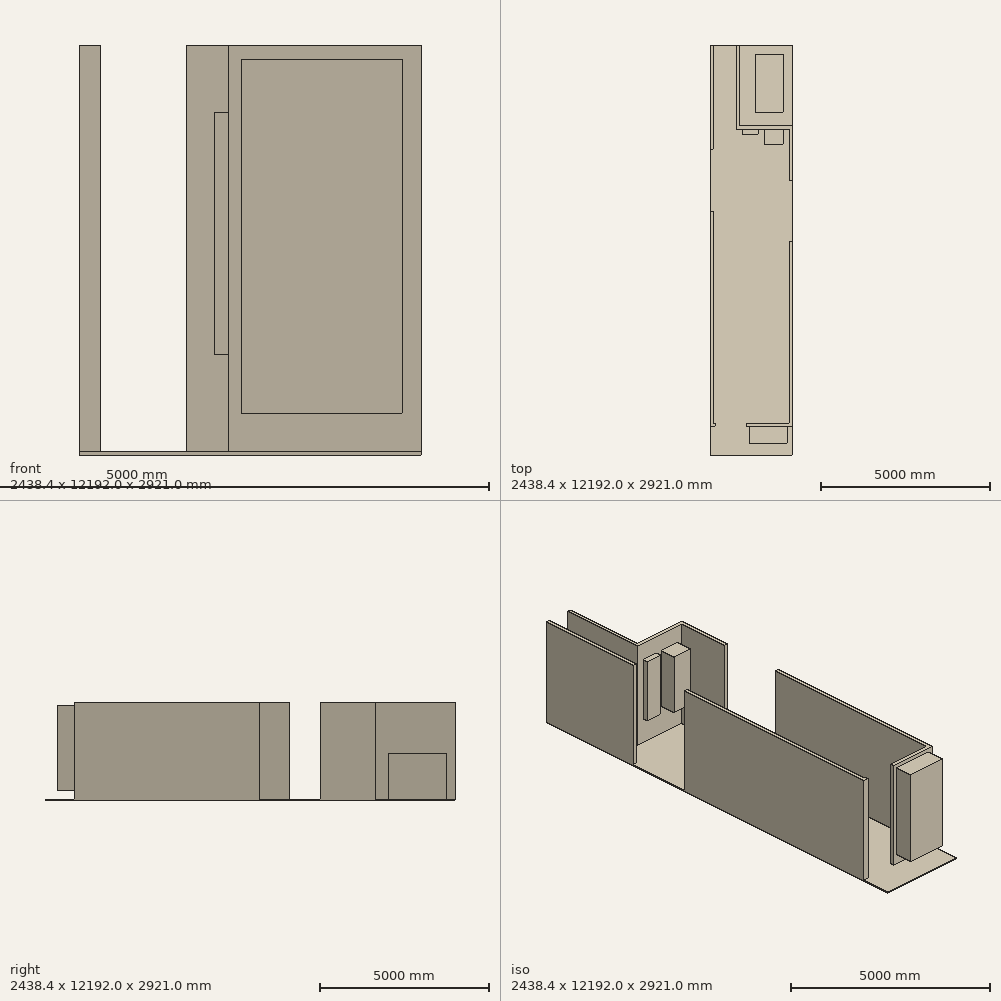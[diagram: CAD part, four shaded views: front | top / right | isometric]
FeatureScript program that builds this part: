
annotation { "Feature Type Name" : "Feature", "Feature Type Description" : "" }
export const myFeature = defineFeature(function(context is Context, id is Id, definition is map)
    precondition{}
    {
        {
            var Q0;
            Q0=qCreatedBy(makeId("Top.planeOp"),FACE);
            var sketch = newSketch(context, id + "F0", { "sketchPlane" : qUnion([Q0])});
            skLineSegment(sketch, "E0.bottom", {"start": v(0, 0) * mm, "end": v(2438.4, 0) * mm});
            skLineSegment(sketch, "E0.top", {"start": v(0, 12192) * mm, "end": v(2438.4, 12192) * mm});
            skLineSegment(sketch, "E0.left", {"start": v(0, 0) * mm, "end": v(0, 12192) * mm});
            skLineSegment(sketch, "E0.right", {"start": v(2438.4, 0) * mm, "end": v(2438.4, 12192) * mm});
            skSolve(sketch);
        }
        {
            var Q0;
            Q0=makeQuery(id+"F0.imprint","IMPRINT",FACE,{"disambiguationData":[TD([[makeQuery(id+"F0.imprint","IMPRINT",EDGE,{"derivedFrom":sQuery(id+"F0.wireOp",EDGE,"E0.bottom")}),1.0]])]});
            extrude(context, id + "F1", {"entities" : qUnion([Q0]), "depth" : 25.4 * mm, "offsetDistance" : 25.4 * mm});
        }
        {
            var Q0;
            Q0=makeQuery(id+"F1.opExtrude","CAP_FACE",FACE,{"disambiguationData":[OSD([sQuery(id+"F0.wireOp",EDGE,"E0.bottom"),sQuery(id+"F0.wireOp",EDGE,"E0.top"),sQuery(id+"F0.wireOp",EDGE,"E0.left"),sQuery(id+"F0.wireOp",EDGE,"E0.right")])],"isStart":false});
            var sketch = newSketch(context, id + "F2", { "sketchPlane" : qUnion([Q0])});
            skLineSegment(sketch, "E1.0", {"start": v(0, 0) * mm, "end": v(0, 7264.4) * mm});
            skLineSegment(sketch, "E2.0", {"start": v(0, 12192) * mm, "end": v(2438.4, 12192) * mm});
            skLineSegment(sketch, "E2.1", {"start": v(2438.4, 0) * mm, "end": v(2438.4, 6350) * mm});
            skLineSegment(sketch, "E2.2", {"start": v(0, 0) * mm, "end": v(2438.4, 0) * mm});
            skLineSegment(sketch, "E3.1", {"start": v(101.6, 965.2) * mm, "end": v(101.6, 7264.4) * mm});
            skLineSegment(sketch, "E4", {"start": v(0, 863.6) * mm, "end": v(149.81, 863.6) * mm});
            skLineSegment(sketch, "E5", {"start": v(762, 12192) * mm, "end": v(762, 9702.8) * mm});
            skLineSegment(sketch, "E6", {"start": v(762, 9702.8) * mm, "end": v(2336.8, 9702.8) * mm});
            skLineSegment(sketch, "E7.0", {"start": v(863.6, 9804.4) * mm, "end": v(2438.4, 9804.4) * mm});
            skLineSegment(sketch, "E7.1", {"start": v(863.6, 12192) * mm, "end": v(863.6, 9804.4) * mm});
            skLineSegment(sketch, "E8.0", {"start": v(101.6, 965.2) * mm, "end": v(149.81, 965.2) * mm});
            skLineSegment(sketch, "E9.trimOffspring", {"start": v(2336.8, 965.2) * mm, "end": v(2336.8, 6350) * mm});
            skLineSegment(sketch, "E10", {"start": v(1064.21, 965.2) * mm, "end": v(1064.21, 863.6) * mm});
            skLineSegment(sketch, "E11", {"start": v(149.81, 965.2) * mm, "end": v(149.81, 863.6) * mm});
            skLineSegment(sketch, "E12", {"start": v(2336.8, 8178.8) * mm, "end": v(2438.4, 8178.8) * mm});
            skLineSegment(sketch, "E13", {"start": v(2336.8, 6350) * mm, "end": v(2438.4, 6350) * mm});
            skLineSegment(sketch, "E14", {"start": v(0, 9093.2) * mm, "end": v(101.6, 9093.2) * mm});
            skLineSegment(sketch, "E15", {"start": v(101.6, 7264.4) * mm, "end": v(0, 7264.4) * mm});
            skLineSegment(sketch, "E16.trimOffspring", {"start": v(0, 9093.2) * mm, "end": v(0, 12192) * mm});
            skLineSegment(sketch, "E17.trimOffspring", {"start": v(101.6, 9093.2) * mm, "end": v(101.6, 12192) * mm});
            skLineSegment(sketch, "E18.trimOffspring", {"start": v(2438.4, 8178.8) * mm, "end": v(2438.4, 12192) * mm});
            skLineSegment(sketch, "E19.trimOffspring", {"start": v(2336.8, 8178.8) * mm, "end": v(2336.8, 9702.8) * mm});
            skLineSegment(sketch, "E20.trimOffspring", {"start": v(1064.21, 965.2) * mm, "end": v(2336.8, 965.2) * mm});
            skLineSegment(sketch, "E21.trimOffspring", {"start": v(1064.21, 863.6) * mm, "end": v(2438.4, 863.6) * mm});
            skSolve(sketch);
        }
        {
            var Q0;
            {var subQ2=sQuery(id+"F2.wireOp",EDGE,"E3.1");Q0=makeQuery(id+"F2.imprint","IMPRINT",FACE,{"disambiguationData":[TD([[makeQuery(id+"F2.imprint","IMPRINT",EDGE,{"derivedFrom":subQ2}),1.0]])]});}
            var Q1;
            Q1=makeQuery(id+"F2.imprint","IMPRINT",FACE,{"disambiguationData":[TD([[makeQuery(id+"F2.imprint","IMPRINT",EDGE,{"derivedFrom":sQuery(id+"F2.wireOp",EDGE,"E14")}),1.0]])]});
            var Q2;
            {var subQ1=sQuery(id+"F2.wireOp",EDGE,"E5");Q2=makeQuery(id+"F2.imprint","IMPRINT",FACE,{"disambiguationData":[TD([[makeQuery(id+"F2.imprint","IMPRINT",EDGE,{"derivedFrom":subQ1}),1.0]])]});}
            var Q3;
            Q3=makeQuery(id+"F2.imprint","IMPRINT",FACE,{"disambiguationData":[TD([[makeQuery(id+"F2.imprint","IMPRINT",EDGE,{"derivedFrom":sQuery(id+"F2.wireOp",EDGE,"E9.trimOffspring")}),-1.0]])]});
            extrude(context, id + "F3", {"entities" : qUnion([Q0, Q1, Q2, Q3]), "operationType" : NewBodyOperationType.ADD, "depth" : 2895.6 * mm, "offsetDistance" : 25.4 * mm});
        }
        {
            var Q0;
            {var subQ2=sQuery(id+"F0.wireOp",EDGE,"E0.right");var subQ3=sQuery(id+"F0.wireOp",EDGE,"E0.top");Q0=makeQuery(id+"F3.boolean.opBoolean","SPLIT",FACE,{"disambiguationData":[TD([makeQuery(id+"F3.opExtrude","SWEPT_FACE",FACE,{"disambiguationData":[OSD([sQuery(id+"F2.wireOp",EDGE,"E7.0")])]})])],"derivedFrom":makeQuery(id+"F1.opExtrude","CAP_FACE",FACE,{"disambiguationData":[OSD([sQuery(id+"F0.wireOp",EDGE,"E0.bottom"),subQ3,sQuery(id+"F0.wireOp",EDGE,"E0.left"),subQ2])],"isStart":false})});}
            var sketch = newSketch(context, id + "F4", { "sketchPlane" : qUnion([Q0])});
            skLineSegment(sketch, "E22.bottom", {"start": v(1328.63, 11909.7) * mm, "end": v(2160.1, 11909.7) * mm});
            skLineSegment(sketch, "E22.top", {"start": v(1328.63, 10187.38) * mm, "end": v(2160.1, 10187.38) * mm});
            skLineSegment(sketch, "E22.left", {"start": v(1328.63, 11909.7) * mm, "end": v(1328.63, 10187.38) * mm});
            skLineSegment(sketch, "E22.right", {"start": v(2160.1, 11909.7) * mm, "end": v(2160.1, 10187.38) * mm});
            skSolve(sketch);
        }
        {
            var Q0;
            Q0=makeQuery(id+"F4.imprint","IMPRINT",FACE,{"disambiguationData":[TD([[makeQuery(id+"F4.imprint","IMPRINT",EDGE,{"derivedFrom":sQuery(id+"F4.wireOp",EDGE,"E22.bottom")}),-1.0]])]});
            extrude(context, id + "F5", {"entities" : qUnion([Q0]), "operationType" : NewBodyOperationType.ADD, "depth" : 1371.6 * mm, "offsetDistance" : 25.4 * mm});
        }
        {
            var Q0;
            Q0=makeQuery(id+"F3.opExtrude","SWEPT_FACE",FACE,{"disambiguationData":[OSD([sQuery(id+"F2.wireOp",EDGE,"E21.trimOffspring")])]});
            var sketch = newSketch(context, id + "F6", { "sketchPlane" : qUnion([Q0])});
            skLineSegment(sketch, "E23.bottom", {"start": v(2299.67, 2820.35) * mm, "end": v(1154.66, 2820.35) * mm});
            skLineSegment(sketch, "E23.top", {"start": v(2299.67, 296.67) * mm, "end": v(1154.66, 296.67) * mm});
            skLineSegment(sketch, "E23.left", {"start": v(2299.67, 2820.35) * mm, "end": v(2299.67, 296.67) * mm});
            skLineSegment(sketch, "E23.right", {"start": v(1154.66, 2820.35) * mm, "end": v(1154.66, 296.67) * mm});
            skSolve(sketch);
        }
        {
            var Q0;
            Q0=makeQuery(id+"F6.imprint","IMPRINT",FACE,{"disambiguationData":[TD([[makeQuery(id+"F6.imprint","IMPRINT",EDGE,{"derivedFrom":sQuery(id+"F6.wireOp",EDGE,"E23.bottom")}),1.0]])]});
            extrude(context, id + "F7", {"entities" : qUnion([Q0]), "operationType" : NewBodyOperationType.ADD, "depth" : 508 * mm, "offsetDistance" : 25.4 * mm});
        }
        {
            var Q0;
            Q0=makeQuery(id+"F3.opExtrude","SWEPT_FACE",FACE,{"disambiguationData":[OSD([sQuery(id+"F2.wireOp",EDGE,"E6")])]});
            var sketch = newSketch(context, id + "F8", { "sketchPlane" : qUnion([Q0])});
            skLineSegment(sketch, "E24.bottom", {"start": v(2183.74, 2442.6) * mm, "end": v(1605.92, 2442.6) * mm});
            skLineSegment(sketch, "E24.top", {"start": v(2183.74, 822.53) * mm, "end": v(1605.92, 822.53) * mm});
            skLineSegment(sketch, "E24.left", {"start": v(2183.74, 2442.6) * mm, "end": v(2183.74, 822.53) * mm});
            skLineSegment(sketch, "E24.right", {"start": v(1605.92, 2442.6) * mm, "end": v(1605.92, 822.53) * mm});
            skSolve(sketch);
        }
        {
            var Q0;
            Q0=makeQuery(id+"F8.imprint","IMPRINT",FACE,{"disambiguationData":[TD([[makeQuery(id+"F8.imprint","IMPRINT",EDGE,{"derivedFrom":sQuery(id+"F8.wireOp",EDGE,"E24.bottom")}),1.0]])]});
            extrude(context, id + "F9", {"entities" : qUnion([Q0]), "operationType" : NewBodyOperationType.ADD, "depth" : 457.2 * mm, "offsetDistance" : 25.4 * mm});
        }
        {
            var Q0;
            Q0=makeQuery(id+"F3.opExtrude","SWEPT_FACE",FACE,{"disambiguationData":[OSD([sQuery(id+"F2.wireOp",EDGE,"E6")])]});
            var sketch = newSketch(context, id + "F10", { "sketchPlane" : qUnion([Q0])});
            skLineSegment(sketch, "E25.bottom", {"start": v(1438.06, 2442.6) * mm, "end": v(960.51, 2442.6) * mm});
            skLineSegment(sketch, "E25.top", {"start": v(1438.06, 718.22) * mm, "end": v(960.51, 718.22) * mm});
            skLineSegment(sketch, "E25.left", {"start": v(1438.06, 2442.6) * mm, "end": v(1438.06, 718.22) * mm});
            skLineSegment(sketch, "E25.right", {"start": v(960.51, 2442.6) * mm, "end": v(960.51, 718.22) * mm});
            skSolve(sketch);
        }
        {
            var Q0;
            Q0=makeQuery(id+"F10.imprint","IMPRINT",FACE,{"disambiguationData":[TD([[makeQuery(id+"F10.imprint","IMPRINT",EDGE,{"derivedFrom":sQuery(id+"F10.wireOp",EDGE,"E25.bottom")}),1.0]])]});
            extrude(context, id + "F11", {"entities" : qUnion([Q0]), "operationType" : NewBodyOperationType.ADD, "depth" : 152.4 * mm, "offsetDistance" : 25.4 * mm});
        }
    });
